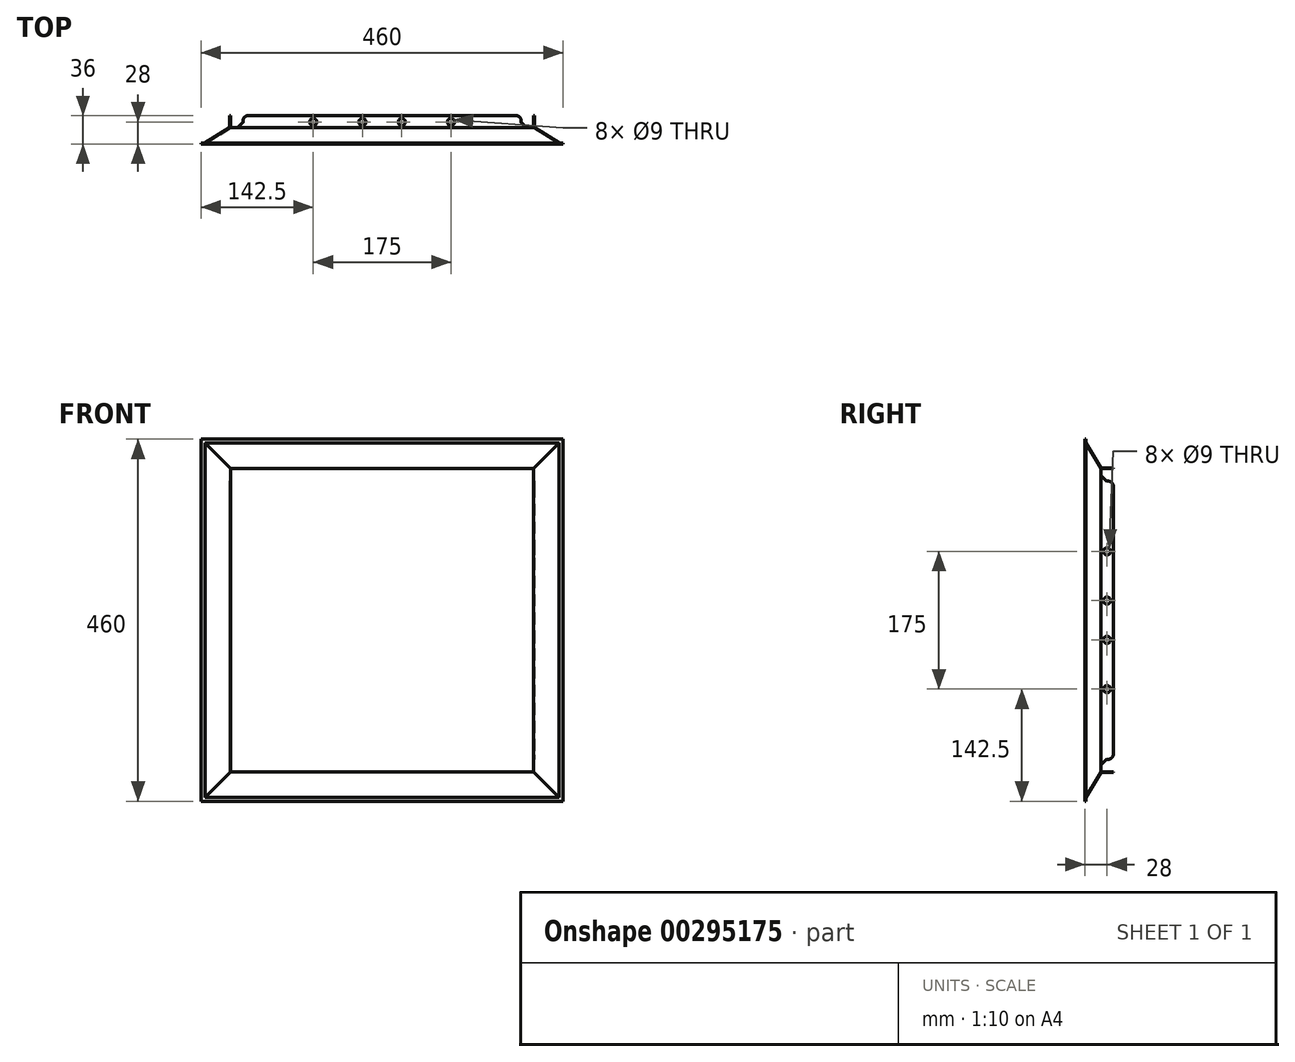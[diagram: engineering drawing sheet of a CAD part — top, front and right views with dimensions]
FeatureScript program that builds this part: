
annotation { "Feature Type Name" : "Feature", "Feature Type Description" : "" }
export const myFeature = defineFeature(function(context is Context, id is Id, definition is map)
    precondition{}
    {
        {
            var Q0;
            Q0=qCreatedBy(makeId("Front.planeOp"),FACE);
            var sketch = newSketch(context, id + "F0", { "sketchPlane" : qUnion([Q0])});
            skLineSegment(sketch, "E0.bottom", {"start": v(230, 230) * mm, "end": v(-230, 230) * mm});
            skLineSegment(sketch, "E0.top", {"start": v(230, -230) * mm, "end": v(-230, -230) * mm});
            skLineSegment(sketch, "E0.left", {"start": v(230, 230) * mm, "end": v(230, -230) * mm});
            skLineSegment(sketch, "E0.right", {"start": v(-230, 230) * mm, "end": v(-230, -230) * mm});
            skPoint(sketch, "E0.middle", {"position": v(0, 0) * mm});
            skLineSegment(sketch, "E1.bottom", {"start": v(-225, 225) * mm, "end": v(225, 225) * mm});
            skLineSegment(sketch, "E1.top", {"start": v(-225, -225) * mm, "end": v(225, -225) * mm});
            skLineSegment(sketch, "E1.left", {"start": v(-225, 225) * mm, "end": v(-225, -225) * mm});
            skLineSegment(sketch, "E1.right", {"start": v(225, 225) * mm, "end": v(225, -225) * mm});
            skSolve(sketch);
        }
        {
            var Q0;
            Q0=qCreatedBy(makeId("Front.planeOp"),FACE);
            cPlane(context, id + "F1", {"entities" : qUnion([Q0]), "cplaneType" : CPlaneType.OFFSET, "offset" : 20 * mm, "oppositeDirection" : true, "width" : 150 * mm, "height" : 150 * mm});
        }
        {
            var Q0;
            Q0=qCreatedBy(id+"F1.planeOp",FACE);
            var sketch = newSketch(context, id + "F2", { "sketchPlane" : qUnion([Q0])});
            skLineSegment(sketch, "E2.bottom", {"start": v(192.5, 192.5) * mm, "end": v(-192.5, 192.5) * mm});
            skLineSegment(sketch, "E2.top", {"start": v(192.5, -192.5) * mm, "end": v(-192.5, -192.5) * mm});
            skLineSegment(sketch, "E2.left", {"start": v(192.5, 192.5) * mm, "end": v(192.5, -192.5) * mm});
            skLineSegment(sketch, "E2.right", {"start": v(-192.5, 192.5) * mm, "end": v(-192.5, -192.5) * mm});
            skPoint(sketch, "E2.middle", {"position": v(0, 0) * mm});
            skSolve(sketch);
        }
        {
            var Q0;
            Q0=makeQuery(id+"F0.imprint","IMPRINT",FACE,{"disambiguationData":[TD([[makeQuery(id+"F0.imprint","IMPRINT",EDGE,{"derivedFrom":sQuery(id+"F0.wireOp",EDGE,"E1.bottom")}),-1.0]])]});
            var Q1;
            Q1=makeQuery(id+"F2.imprint","IMPRINT",FACE,{"disambiguationData":[TD([[makeQuery(id+"F2.imprint","IMPRINT",EDGE,{"derivedFrom":sQuery(id+"F2.wireOp",EDGE,"E2.bottom")}),1.0]])]});
            loft(context, id + "F3", {"sheetProfilesArray" : [{ "sheetProfileEntities" : qUnion([Q0]) }, { "sheetProfileEntities" : qUnion([Q1]) }]});
        }
        {
            var Q0;
            Q0=qCreatedBy(id+"F1.planeOp",FACE);
            cPlane(context, id + "F4", {"entities" : qUnion([Q0]), "cplaneType" : CPlaneType.OFFSET, "offset" : 16 * mm, "oppositeDirection" : true, "width" : 150 * mm, "height" : 150 * mm});
        }
        {
            var Q0;
            Q0=qCreatedBy(id+"F4.planeOp",FACE);
            var sketch = newSketch(context, id + "F5", { "sketchPlane" : qUnion([Q0])});
            skLineSegment(sketch, "E3.0.0", {"start": v(192.5, -192.5) * mm, "end": v(-192.5, -192.5) * mm});
            skLineSegment(sketch, "E3.0.1", {"start": v(-192.5, -192.5) * mm, "end": v(-192.5, 192.5) * mm});
            skLineSegment(sketch, "E3.0.2", {"start": v(-192.5, 192.5) * mm, "end": v(192.5, 192.5) * mm});
            skLineSegment(sketch, "E3.0.3", {"start": v(192.5, 192.5) * mm, "end": v(192.5, -192.5) * mm});
            skSolve(sketch);
        }
        {
            var Q1;
            Q1=makeQuery(id+"F5.imprint","IMPRINT",FACE,{"disambiguationData":[TD([[makeQuery(id+"F5.imprint","IMPRINT",EDGE,{"derivedFrom":sQuery(id+"F5.wireOp",EDGE,"E3.0.0")}),-1.0]])]});
            var Q2;
            Q2=makeQuery(id+"F3.opLoft","CAP_FACE",FACE,{"disambiguationData":[OSD([makeQuery(id+"F2.imprint","IMPRINT",FACE,{"disambiguationData":[TD([[makeQuery(id+"F2.imprint","IMPRINT",EDGE,{"derivedFrom":sQuery(id+"F2.wireOp",EDGE,"E2.bottom")}),1.0]])]})])],"isStart":true});
            loft(context, id + "F6", {"operationType" : NewBodyOperationType.ADD, "sheetProfilesArray" : [{ "sheetProfileEntities" : qUnion([Q1]) }, { "sheetProfileEntities" : qUnion([Q2]) }]});
        }
        {
            var Q0;
            Q0=makeQuery(id+"F3.opLoft","CAP_FACE",FACE,{"disambiguationData":[OSD([makeQuery(id+"F0.imprint","IMPRINT",FACE,{"disambiguationData":[TD([[makeQuery(id+"F0.imprint","IMPRINT",EDGE,{"derivedFrom":sQuery(id+"F0.wireOp",EDGE,"E1.bottom")}),-1.0]])]})])],"isStart":true});
            var Q1;
            Q1=makeQuery(id+"F6.opLoft","CAP_FACE",FACE,{"disambiguationData":[OSD([makeQuery(id+"F5.imprint","IMPRINT",FACE,{"disambiguationData":[TD([[makeQuery(id+"F5.imprint","IMPRINT",EDGE,{"derivedFrom":sQuery(id+"F5.wireOp",EDGE,"E3.0.0")}),-1.0]])]})])],"isStart":true});
            shell(context, id + "F7", {"entities" : qUnion([Q0, Q1]), "thickness" : 1 * mm, "oppositeDirection" : true});
        }
        {
            var Q0;
            Q0=makeQuery(id+"F6.opLoft","SWEPT_FACE",FACE,{"disambiguationData":[OSD([sQuery(id+"F2.wireOp",EDGE,"E2.bottom"),sQuery(id+"F2.wireOp",EDGE,"E2.top"),sQuery(id+"F2.wireOp",EDGE,"E2.right"),sQuery(id+"F5.wireOp",EDGE,"E3.0.0"),sQuery(id+"F5.wireOp",EDGE,"E3.0.1"),sQuery(id+"F5.wireOp",EDGE,"E3.0.2")])]});
            var sketch = newSketch(context, id + "F8", { "sketchPlane" : qUnion([Q0])});
            skLineSegment(sketch, "E4", {"start": v(-20.56, 193.5) * mm, "end": v(-20.56, 183.5) * mm});
            skLineSegment(sketch, "E5", {"start": v(-20.56, 183.5) * mm, "end": v(-27.63, 176.43) * mm});
            skArc(sketch, "E6", {"start": v(-27.63, 176.43) * mm, "mid": v(-33.79, 175.02) * mm, "end": v(-36, 169.1) * mm});
            skLineSegment(sketch, "E7", {"start": v(-20.56, 193.5) * mm, "end": v(-36, 193.5) * mm});
            skLineSegment(sketch, "E8", {"start": v(-36, 193.5) * mm, "end": v(-36, 169.1) * mm});
            skLineSegment(sketch, "E9.MirrorCS", {"start": v(-20.56, -193.5) * mm, "end": v(-36, -193.5) * mm});
            skArc(sketch, "E10.MirrorCS", {"start": v(-27.63, -176.43) * mm, "mid": v(-33.79, -175.02) * mm, "end": v(-36, -169.1) * mm});
            skLineSegment(sketch, "E11.MirrorCS", {"start": v(-20.56, -193.5) * mm, "end": v(-20.56, -183.5) * mm});
            skLineSegment(sketch, "E12.MirrorCS", {"start": v(-20.56, -183.5) * mm, "end": v(-27.63, -176.43) * mm});
            skLineSegment(sketch, "E13.MirrorCS", {"start": v(-36, -193.5) * mm, "end": v(-36, -169.1) * mm});
            skSolve(sketch);
        }
        {
            var Q0;
            Q0=makeQuery(id+"F8.imprint","IMPRINT",FACE,{"disambiguationData":[TD([[makeQuery(id+"F8.imprint","IMPRINT",EDGE,{"derivedFrom":sQuery(id+"F8.wireOp",EDGE,"E4")}),1.0]])]});
            var Q1;
            Q1=sQuery(id+"F8.wireOp",EDGE,"E7");
            revolve(context, id + "F9", {"operationType" : NewBodyOperationType.REMOVE, "entities" : qUnion([Q0]), "axis" : qUnion([Q1]), "revolveType" : RevolveType.FULL, "oppositeDirection" : true});
        }
        {
            var Q0;
            {var subQ4=sQuery(id+"F8.wireOp",EDGE,"E9.MirrorCS");Q0=makeQuery(id+"F8.imprint","IMPRINT",FACE,{"disambiguationData":[TD([[makeQuery(id+"F8.imprint","IMPRINT",EDGE,{"derivedFrom":subQ4}),1.0]])]});}
            var Q1;
            Q1=sQuery(id+"F8.wireOp",EDGE,"E9.MirrorCS");
            revolve(context, id + "F10", {"operationType" : NewBodyOperationType.REMOVE, "entities" : qUnion([Q0]), "axis" : qUnion([Q1]), "revolveType" : RevolveType.FULL, "oppositeDirection" : true});
        }
        {
            var Q0;
            Q0=makeQuery(id+"F6.opLoft","SWEPT_FACE",FACE,{"disambiguationData":[OSD([sQuery(id+"F2.wireOp",EDGE,"E2.bottom"),sQuery(id+"F2.wireOp",EDGE,"E2.top"),sQuery(id+"F2.wireOp",EDGE,"E2.left"),sQuery(id+"F5.wireOp",EDGE,"E3.0.0"),sQuery(id+"F5.wireOp",EDGE,"E3.0.2"),sQuery(id+"F5.wireOp",EDGE,"E3.0.3")])]});
            var sketch = newSketch(context, id + "F11", { "sketchPlane" : qUnion([Q0])});
            skLineSegment(sketch, "E14.0", {"start": v(20.56, -183.5) * mm, "end": v(27.63, -176.43) * mm});
            skArc(sketch, "E15.0", {"start": v(27.63, -176.43) * mm, "mid": v(33.79, -175.02) * mm, "end": v(36, -169.1) * mm});
            skLineSegment(sketch, "E16.0", {"start": v(20.56, -193.5) * mm, "end": v(20.56, -183.5) * mm});
            skLineSegment(sketch, "E17.0", {"start": v(20.56, -193.5) * mm, "end": v(36, -193.5) * mm});
            skLineSegment(sketch, "E18.0", {"start": v(36, -193.5) * mm, "end": v(36, -169.1) * mm});
            skLineSegment(sketch, "E19.MirrorCS", {"start": v(20.56, 193.5) * mm, "end": v(20.56, 183.5) * mm});
            skLineSegment(sketch, "E20.MirrorCS", {"start": v(20.56, 193.5) * mm, "end": v(36, 193.5) * mm});
            skLineSegment(sketch, "E21.MirrorCS", {"start": v(20.56, 183.5) * mm, "end": v(27.63, 176.43) * mm});
            skLineSegment(sketch, "E22.MirrorCS", {"start": v(36, 193.5) * mm, "end": v(36, 169.1) * mm});
            skArc(sketch, "E23.MirrorCS", {"start": v(27.63, 176.43) * mm, "mid": v(33.79, 175.02) * mm, "end": v(36, 169.1) * mm});
            skSolve(sketch);
        }
        {
            var Q0;
            {var subQ2=sQuery(id+"F11.wireOp",EDGE,"E14.0");Q0=makeQuery(id+"F11.imprint","IMPRINT",FACE,{"disambiguationData":[TD([[makeQuery(id+"F11.imprint","IMPRINT",EDGE,{"derivedFrom":subQ2}),-1.0]])]});}
            var Q1;
            Q1=sQuery(id+"F11.wireOp",EDGE,"E17.0");
            revolve(context, id + "F12", {"operationType" : NewBodyOperationType.REMOVE, "entities" : qUnion([Q0]), "axis" : qUnion([Q1]), "revolveType" : RevolveType.FULL, "oppositeDirection" : true});
        }
        {
            var Q0;
            Q0=makeQuery(id+"F11.imprint","IMPRINT",FACE,{"disambiguationData":[TD([[makeQuery(id+"F11.imprint","IMPRINT",EDGE,{"derivedFrom":sQuery(id+"F11.wireOp",EDGE,"E19.MirrorCS")}),1.0]])]});
            var Q1;
            Q1=sQuery(id+"F11.wireOp",EDGE,"E20.MirrorCS");
            revolve(context, id + "F13", {"operationType" : NewBodyOperationType.REMOVE, "entities" : qUnion([Q0]), "axis" : qUnion([Q1]), "revolveType" : RevolveType.FULL, "oppositeDirection" : true});
        }
        {
            var Q0;
            Q0=makeQuery(id+"F6.opLoft","SWEPT_FACE",FACE,{"disambiguationData":[OSD([sQuery(id+"F2.wireOp",EDGE,"E2.top"),sQuery(id+"F2.wireOp",EDGE,"E2.left"),sQuery(id+"F2.wireOp",EDGE,"E2.right"),sQuery(id+"F5.wireOp",EDGE,"E3.0.0"),sQuery(id+"F5.wireOp",EDGE,"E3.0.1"),sQuery(id+"F5.wireOp",EDGE,"E3.0.3")])]});
            var sketch = newSketch(context, id + "F14", { "sketchPlane" : qUnion([Q0])});
            skCircle(sketch, "E24", {"center": v(-25, -28) * mm, "radius": 4.5 * mm});
            skCircle(sketch, "E25", {"center": v(25, -28) * mm, "radius": 4.5 * mm});
            skCircle(sketch, "E26", {"center": v(-87.5, -28) * mm, "radius": 4.5 * mm});
            skCircle(sketch, "E27", {"center": v(87.5, -28) * mm, "radius": 4.5 * mm});
            skSolve(sketch);
        }
        {
            var Q0;
            Q0=qSketchRegion(id+"F14",true);
            extrude(context, id + "F15", {"entities" : qUnion([Q0]), "operationType" : NewBodyOperationType.REMOVE, "endBound" : BoundingType.THROUGH_ALL, "oppositeDirection" : true, "depth" : 25 * mm});
        }
        {
            var Q0;
            Q0=makeQuery(id+"F6.opLoft","SWEPT_FACE",FACE,{"disambiguationData":[OSD([sQuery(id+"F2.wireOp",EDGE,"E2.bottom"),sQuery(id+"F2.wireOp",EDGE,"E2.top"),sQuery(id+"F2.wireOp",EDGE,"E2.right"),sQuery(id+"F5.wireOp",EDGE,"E3.0.0"),sQuery(id+"F5.wireOp",EDGE,"E3.0.1"),sQuery(id+"F5.wireOp",EDGE,"E3.0.2")])]});
            var sketch = newSketch(context, id + "F16", { "sketchPlane" : qUnion([Q0])});
            skCircle(sketch, "E28", {"center": v(-28, 25) * mm, "radius": 4.5 * mm});
            skCircle(sketch, "E29", {"center": v(-28, 87.5) * mm, "radius": 4.5 * mm});
            skCircle(sketch, "E30.MirrorC", {"center": v(-28, -25) * mm, "radius": 4.5 * mm});
            skCircle(sketch, "E31.MirrorC", {"center": v(-28, -87.5) * mm, "radius": 4.5 * mm});
            skSolve(sketch);
        }
        {
            var Q0;
            Q0=qSketchRegion(id+"F16",true);
            extrude(context, id + "F17", {"entities" : qUnion([Q0]), "operationType" : NewBodyOperationType.REMOVE, "endBound" : BoundingType.THROUGH_ALL, "oppositeDirection" : true, "depth" : 25 * mm});
        }
        {
            var Q0;
            Q0=qCreatedBy(makeId("Right.planeOp"),FACE);
            var sketch = newSketch(context, id + "F18", { "sketchPlane" : qUnion([Q0])});
            skLineSegment(sketch, "E32.bottom", {"start": v(0, 230) * mm, "end": v(1, 230) * mm});
            skLineSegment(sketch, "E32.top", {"start": v(0, 225) * mm, "end": v(1, 225) * mm});
            skLineSegment(sketch, "E32.left", {"start": v(0, 230) * mm, "end": v(0, 225) * mm});
            skLineSegment(sketch, "E32.right", {"start": v(1, 230) * mm, "end": v(1, 225) * mm});
            skSolve(sketch);
        }
        {
            var Q0;
            Q0=makeQuery(id+"F18.imprint","IMPRINT",FACE,{"disambiguationData":[TD([[makeQuery(id+"F18.imprint","IMPRINT",EDGE,{"derivedFrom":sQuery(id+"F18.wireOp",EDGE,"E32.bottom")}),-1.0]])]});
            var Q1;
            Q1=makeQuery(id+"F3.opLoft","MID_CAP_EDGE",EDGE,{"disambiguationData":[OSD([sQuery(id+"F0.wireOp",EDGE,"E1.bottom"),sQuery(id+"F0.wireOp",EDGE,"E1.top"),sQuery(id+"F0.wireOp",EDGE,"E1.left")])],"capPos":0.0});
            var Q2;
            Q2=makeQuery(id+"F3.opLoft","MID_CAP_EDGE",EDGE,{"disambiguationData":[OSD([sQuery(id+"F0.wireOp",EDGE,"E1.top"),sQuery(id+"F0.wireOp",EDGE,"E1.left"),sQuery(id+"F0.wireOp",EDGE,"E1.right")])],"capPos":0.0});
            var Q3;
            Q3=makeQuery(id+"F3.opLoft","MID_CAP_EDGE",EDGE,{"disambiguationData":[OSD([sQuery(id+"F0.wireOp",EDGE,"E1.bottom"),sQuery(id+"F0.wireOp",EDGE,"E1.left"),sQuery(id+"F0.wireOp",EDGE,"E1.right")])],"capPos":0.0});
            var Q4;
            Q4=makeQuery(id+"F3.opLoft","MID_CAP_EDGE",EDGE,{"disambiguationData":[OSD([sQuery(id+"F0.wireOp",EDGE,"E1.bottom"),sQuery(id+"F0.wireOp",EDGE,"E1.top"),sQuery(id+"F0.wireOp",EDGE,"E1.right")])],"capPos":0.0});
            sweep(context, id + "F19", {"operationType" : NewBodyOperationType.ADD, "profiles" : qUnion([Q0]), "path" : qUnion([Q1, Q2, Q3, Q4])});
        }
    });
